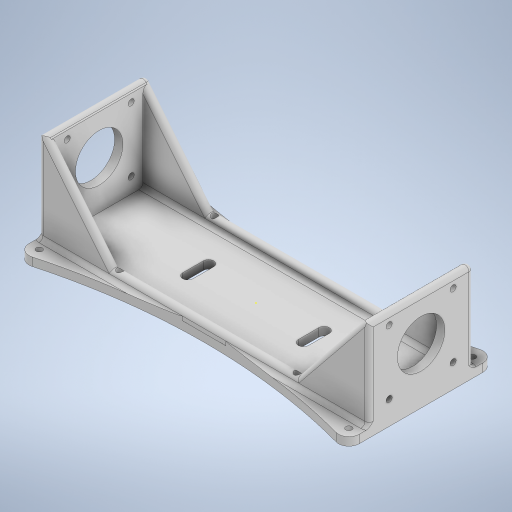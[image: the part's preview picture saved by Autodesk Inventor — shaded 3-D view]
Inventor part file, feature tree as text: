
AUTODESK INVENTOR PART (.ipt)
format: ipt  version: 2023 (Build 270158000, 158)  size: 483,840 bytes
history: native  units: mm
features: sketch x9, extrude x4, hole x4, mirror x3, fillet x3, chamfer x1, projected_geometry x1
ambient origin geometry x8: Origin, YZ Plane, XZ Plane, XY Plane, X Axis, Y Axis, Z Axis, Center Point
bodies: Solid1 (feature_tree)
feature tree (25):
  extrude  "Extrusion1"  Depth=4.0mm TaperAngle=0.0deg
  extrude  "Extrusion3"  Depth=4.0mm
  extrude  "Extrusion4"  Depth=4.0mm
  chamfer  "Chamfer2"  Distance=4.0mm
  mirror  "Mirror2"
  hole  "Hole1"  [1 undecoded]
  hole  "Hole2"  [1 undecoded]
  mirror  "Mirror3"
  extrude  "Extrusion5"  Depth=15.5mm
  mirror  "Mirror4"
  sketch  "Sketch12"  dims[d37=15.5mm d38=15.5mm d39=40.0mm d41=360.0deg]
  fillet  "Fillet10"  Radius=40.0mm
  hole  "Hole3"  [1 undecoded]
  hole  "Hole4"  [1 undecoded]
  fillet  "Fillet12"  Radius=40.0mm
  fillet  "Fillet13"  Radius=60.0mm
  sketch  "Sketch1"  dims[d1=160.0mm d2=4.0mm d3=0.0mm]
  sketch  "Sketch2"  dims[d6=50.4mm d7=4.0mm]
  sketch  "Sketch5"  dims[d23=4.0mm d24=4.0mm]
  projected_geometry  "Projected Loop1"
  sketch  "Sketch7"  dims[d25=4.0mm d26=4.0mm d27=0.0mm]
  sketch  "Sketch8"  dims[d28=35.0mm d29=42.0mm d30=0.0mm]
  sketch  "Sketch9"  dims[d31=34.0mm d32=42.0mm d33=45.0deg d36=23.0mm]
  sketch  "Sketch13"  dims[d43=2.9mm d44=6.0mm d45=4.4mm d46=2.0mm d47=90.0deg d48=8.0mm d49=20.594885mm d50=23.0mm]
  sketch  "Sketch14"  dims[d51=23.0mm d52=6.0mm d53=20.0mm d54=2.0mm d55=90.0deg d56=8.0mm d57=20.594885mm d61=10.0mm d63=40.0mm d64=0.0mm d71=60.0mm d73=5.0mm d74=50.0mm d75=2.0mm d76=2.9mm d77=6.0mm d78=5.5mm d79=2.0mm d80=90.0deg d81=8.0mm d82=20.594885mm d85=5.0mm d99=46.0mm d100=86.0mm d101=2.9mm d102=6.0mm d103=4.0mm d104=2.0mm d105=90.0deg d106=8.0mm d107=20.594885mm d109=28.0mm d110=2.0mm d111=2.0mm d15=0.0mm d16=0.0mm d17=0.0mm d18=0.0mm d34=0.0mm d35=0.0mm d112=0.0mm d113=0.0mm d114=0.0mm]
note: 4 required parameter values undecoded (feature->parameter linkage not recoverable at this tier; creation-order binding heuristic only, values carry confidence <= 0.55)
